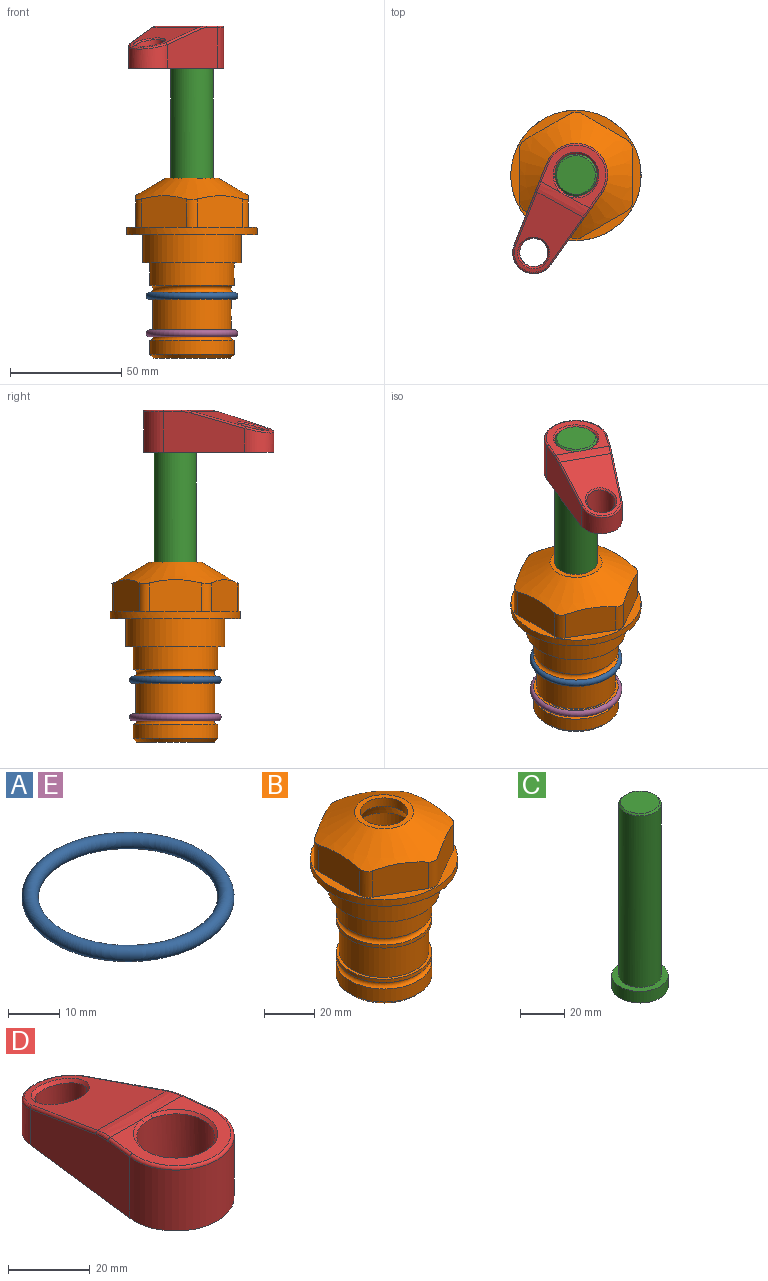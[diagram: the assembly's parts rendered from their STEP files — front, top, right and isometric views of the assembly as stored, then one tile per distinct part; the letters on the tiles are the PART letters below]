
ASSEMBLY  parts=5 mates=4
PART A: 1 faces, bbox 44.7x44.7x3.2 mm
  f0: torus R=19.05mm, axis (0,0,1), area 1193.9mm2
PART B: 36 faces, bbox 58.7x58.7x81 mm
  f0: cylinder r=17.78mm len=35.56mm, axis (0,0,1), area 1670.8mm2, adj f23,f24,f31
  f1: cylinder r=19.05mm len=38.1mm, axis (0,0,1), area 1191.9mm2, adj f26,f27,f30
  f2: plane 58.66x58.66mm, normal (0,0,-1), area 1150.6mm2, adj f3,f28
  f3: cylinder r=29.33mm len=58.66mm, axis (0,0,-1), area 585.1mm2, adj f2,f4
  f4: plane 58.66x58.66mm, normal (0,0,1), area 475.9mm2, adj f3,f5,f6,f7,f8,f9,f10,f11
  f5: plane 20.32x14.34mm, normal (-0.5,0.87,0), area 324.4mm2, adj f4,f15,f16,f17
  f6: plane 20.32x14.34mm, normal (0.5,0.87,0), area 324.4mm2, adj f4,f14,f15,f17
  f7: plane 23.48x14.34mm, normal (1,0,0), area 324.4mm2, adj f4,f13,f14,f17
  f8: plane 20.32x14.34mm, normal (0.5,-0.87,0), area 324.4mm2, adj f4,f12,f13,f17
  f9: plane 20.32x14.34mm, normal (-0.5,-0.87,0), area 324.4mm2, adj f4,f11,f12,f17
  f10: plane 23.48x14.34mm, normal (-1,0,0), area 324.4mm2, adj f4,f11,f16,f17
  f11: cylinder r=5.08mm len=12.85mm, axis (0,0,-1), area 67.2mm2, adj f4,f9,f10,f17
  f12: cylinder r=5.08mm len=12.85mm, axis (0,0,-1), area 67.2mm2, adj f4,f8,f9,f17
  f13: cylinder r=5.08mm len=12.85mm, axis (0,0,-1), area 67.2mm2, adj f4,f7,f8,f17
  f14: cylinder r=5.08mm len=12.85mm, axis (0,0,-1), area 67.2mm2, adj f4,f6,f7,f17
  f15: cylinder r=5.08mm len=12.85mm, axis (0,0,-1), area 67.2mm2, adj f4,f5,f6,f17
  f16: cylinder r=5.08mm len=12.85mm, axis (0,0,-1), area 67.2mm2, adj f4,f5,f10,f17
  f17: cone r=11.73mm half-angle=60deg, axis (0,0,-1), area 2071.8mm2, adj f5,f6,f7,f8,f9,f10,f11,f12
  f18: plane 23.46x23.46mm, normal (0,0,1), area 147.4mm2, adj f17,f35
  f19: plane 34.93x34.93mm, normal (0,0,-1), area 958mm2, adj f29
  f20: cylinder r=19.05mm len=38.1mm, axis (0,0,1), area 760.1mm2, adj f21,f29
  f21: torus R=19.05mm, axis (0,0,1), area 565.3mm2, adj f20,f22
  f22: cylinder r=19.05mm len=38.1mm, axis (0,0,1), area 190mm2, adj f21,f23
  f23: plane 38.1x38.1mm, normal (0,0,1), area 146.9mm2, adj f0,f22
  f24: plane 38.1x38.1mm, normal (0,0,-1), area 146.9mm2, adj f0,f25
  f25: cylinder r=19.05mm len=38.1mm, axis (0,0,1), area 190mm2, adj f24,f26
  f26: torus R=19.05mm, axis (0,0,1), area 565.3mm2, adj f1,f25
  f27: plane 44.45x44.45mm, normal (0,0,-1), area 411.7mm2, adj f1,f28
  f28: cylinder r=22.23mm len=44.45mm, axis (0,0,1), area 1773.5mm2, adj f2,f27
  f29: cone r=19.05mm half-angle=45deg, axis (0,0,1), area 257.5mm2, adj f19,f20
  f30: cylinder r=3.17mm len=6.75mm, axis (-1,0,0), area 128mm2, adj f1,f33
  f31: cylinder r=3.17mm len=6.35mm, axis (-1,0,0), area 102.5mm2, adj f0,f33
  f32: plane 25.4x25.4mm, normal (0,0,1), area 506.7mm2, adj f33
  f33: cylinder r=12.7mm len=66.42mm, axis (0,0,-1), area 5236.2mm2, adj f30,f31,f32,f34
  f34: cone r=9.53mm half-angle=30deg, axis (0,0,-1), area 443.4mm2, adj f33,f35
  f35: cylinder r=9.53mm len=19.05mm, axis (0,0,-1), area 240.9mm2, adj f18,f34
PART C: 6 faces, bbox 25.4x25.4x101.6 mm
  f0: plane 17.46x17.46mm, normal (0,0,1), area 239.5mm2, adj f5
  f1: plane 25.4x25.4mm, normal (0,0,-1), area 506.7mm2, adj f2
  f2: cylinder r=12.7mm len=25.4mm, axis (0,0,1), area 506.7mm2, adj f1,f3
  f3: plane 25.4x25.4mm, normal (0,0,1), area 221.7mm2, adj f2,f4
  f4: cylinder r=9.53mm len=94.46mm, axis (0,0,1), area 5653mm2, adj f3,f5
  f5: cone r=8.73mm half-angle=45deg, axis (0,0,-1), area 64.4mm2, adj f0,f4
PART D: 31 faces, bbox 31.7x65.5x19.8 mm
  f0: plane 39.12x18.26mm, normal (0.99,0.12,0), area 612.2mm2, adj f1,f4,f7,f11,f13,f15
  f1: cylinder r=9.53mm len=18.91mm, axis (0,0,-1), area 296.1mm2, adj f0,f2,f7,f17
  f2: plane 39.12x18.26mm, normal (-0.99,0.12,0), area 612.2mm2, adj f1,f4,f7,f12,f14,f16
  f3: cylinder r=6.35mm len=12.7mm, axis (0,0,-1), area 362.4mm2, adj f7,f18
  f4: cylinder r=14.29mm len=28.58mm, axis (0,0,-1), area 882.2mm2, adj f0,f2,f7,f10
  f5: cylinder r=9.53mm len=19.05mm, axis (0,0,-1), area 1092.6mm2, adj f7,f19,f20
  f6: plane 26.99x23.69mm, normal (0,0,1), area 216.2mm2, adj f9,f10,f11,f12,f19
  f7: plane 63.5x28.58mm, normal (0,0,-1), area 661.8mm2, adj f0,f1,f2,f3,f4,f5,f22,f23
  f8: plane 33.52x23.6mm, normal (0,0.26,0.97), area 486mm2, adj f9,f15,f16,f17,f18
  f9: cylinder r=19.05mm len=24.72mm, axis (1,0,0), area 120.4mm2, adj f6,f8,f13,f14,f20
  f10: torus R=13.49mm, axis (0,0,1), area 59mm2, adj f4,f6,f11,f12
  f11: cylinder r=0.79mm len=8.67mm, axis (0.12,-0.99,0), area 10.8mm2, adj f0,f6,f10,f13
  f12: cylinder r=0.79mm len=8.67mm, axis (0.12,0.99,0), area 10.8mm2, adj f2,f6,f10,f14
  f13: bspline ~4.95x1.42mm, area 6.1mm2, adj f0,f9,f11,f15
  f14: bspline ~4.95x1.42mm, area 6.1mm2, adj f2,f9,f12,f16
  f15: cylinder r=0.79mm len=25.95mm, axis (0.12,-0.96,0.26), area 32.9mm2, adj f0,f8,f13,f17
  f16: cylinder r=0.79mm len=25.95mm, axis (0.12,0.96,-0.26), area 32.9mm2, adj f2,f8,f14,f17
  f17: bspline ~18.91x8.38mm, area 30mm2, adj f1,f8,f15,f16
  f18: bspline ~14.29x14.29mm, area 48.3mm2, adj f3,f8
  f19: cone r=9.53mm half-angle=45deg, axis (0,0,1), area 66.5mm2, adj f5,f6,f20
  f20: bspline ~3.22x0.96mm, area 3.5mm2, adj f5,f9,f19
  f21: plane 2.75x2.72mm, normal (0,0,-1), area 2.9mm2, adj f23,f25,f28
  f22: plane 23.05x15.88mm, normal (-0.99,-0.12,0), area 323.6mm2, adj f7,f25,f26,f27,f28,f29
  f23: plane 23.05x15.88mm, normal (0.99,-0.12,0), area 323.6mm2, adj f7,f21,f25,f27,f28,f30
  f24: cylinder r=9.53mm len=10.69mm, axis (0,0,-1), area 114.7mm2, adj f7,f27,f29,f30
  f25: cylinder r=12.7mm len=20.59mm, axis (0,0,-1), area 381.1mm2, adj f7,f21,f22,f23,f26,f28
  f26: plane 2.75x2.72mm, normal (0,0,-1), area 2.9mm2, adj f22,f25,f28
  f27: plane 19.72x18.37mm, normal (0,-0.26,-0.97), area 291.8mm2, adj f22,f23,f24,f28,f29,f30
  f28: cylinder r=15.88mm len=19.92mm, axis (1,0,0), area 54.8mm2, adj f21,f22,f23,f25,f26,f27
  f29: cylinder r=1.59mm len=11mm, axis (0,0,-1), area 34.7mm2, adj f7,f22,f24,f27
  f30: cylinder r=1.59mm len=11mm, axis (0,0,-1), area 34.7mm2, adj f7,f23,f24,f27
PART E: same geometry as A
PLACE A t=(0,0,-3.18)mm
PLACE B at identity fixed
PLACE C rot(axis=(0,0,1),151.4deg) t=(0,0,30.41)mm
PLACE D rot(axis=(0,0,1),151.4deg) t=(0,0,30.41)mm
PLACE E t=(0,0,-20)mm
MATE fastened E.f0 <-> B.f0  axis (0,0,1) through (0,0,-44.51)mm
MATE cylindrical C.f2 <-> B.f0  axis (0,0,-1) through (0,0,-7.69)mm
MATE fastened A.f0 <-> B.f0  axis (0,0,1) through (0,0,-27.69)mm
MATE fastened D.f4 <-> C.f2  axis (0,0,1) through (0,0,93.91)mm
